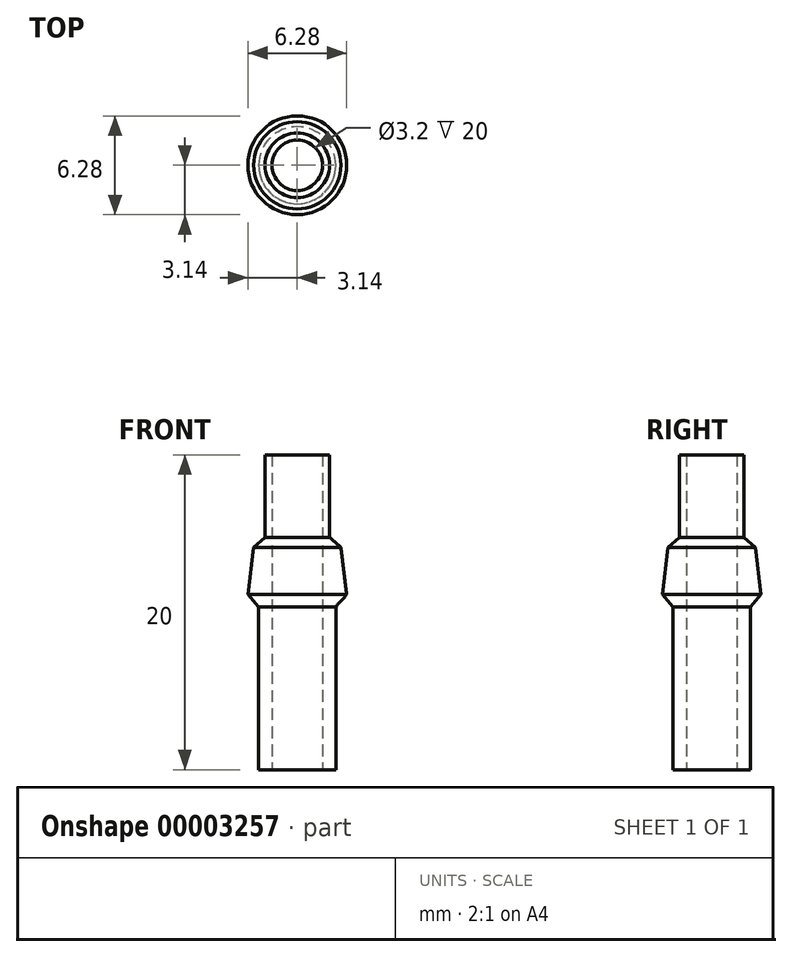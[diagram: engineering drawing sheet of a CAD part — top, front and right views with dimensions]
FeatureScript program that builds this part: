
annotation { "Feature Type Name" : "Feature", "Feature Type Description" : "" }
export const myFeature = defineFeature(function(context is Context, id is Id, definition is map)
    precondition{}
    {
        {
            var Q0;
            Q0=qCreatedBy(makeId("Top.planeOp"),FACE);
            var sketch = newSketch(context, id + "F0", { "sketchPlane" : qUnion([Q0])});
            skCircle(sketch, "E0", {"center": v(0, 0) * mm, "radius": 4.5 * mm});
            skSolve(sketch);
        }
        {
            var Q0;
            Q0=qCreatedBy(makeId("Top.planeOp"),FACE);
            cPlane(context, id + "F1", {"entities" : qUnion([Q0]), "cplaneType" : CPlaneType.OFFSET, "offset" : 20 * mm, "width" : 150 * mm, "height" : 150 * mm});
        }
        {
            var Q0;
            Q0=qCreatedBy(id+"F1.planeOp",FACE);
            var sketch = newSketch(context, id + "F2", { "sketchPlane" : qUnion([Q0])});
            skCircle(sketch, "E1", {"center": v(0, 0) * mm, "radius": 2.05 * mm});
            skSolve(sketch);
        }
        {
            var Q0;
            Q0=makeQuery(id+"F0.imprint","IMPRINT",FACE,{"disambiguationData":[TD([[makeQuery(id+"F0.imprint","IMPRINT",EDGE,{"derivedFrom":sQuery(id+"F0.wireOp",EDGE,"E0")}),1.0]])]});
            var Q1;
            Q1=makeQuery(id+"F2.imprint","IMPRINT",FACE,{"disambiguationData":[TD([[makeQuery(id+"F2.imprint","IMPRINT",EDGE,{"derivedFrom":sQuery(id+"F2.wireOp",EDGE,"E1")}),1.0]])]});
            loft(context, id + "F3", {"sheetProfilesArray" : [{ "sheetProfileEntities" : qUnion([Q0]) }, { "sheetProfileEntities" : qUnion([Q1]) }]});
        }
        {
            var Q0;
            Q0=makeQuery(id+"F3.opLoft","CAP_FACE",FACE,{"disambiguationData":[OSD([makeQuery(id+"F0.imprint","IMPRINT",FACE,{"disambiguationData":[TD([[makeQuery(id+"F0.imprint","IMPRINT",EDGE,{"derivedFrom":sQuery(id+"F0.wireOp",EDGE,"E0")}),1.0]])]})])],"isStart":true});
            var sketch = newSketch(context, id + "F4", { "sketchPlane" : qUnion([Q0])});
            skCircle(sketch, "E2", {"center": v(0, 0) * mm, "radius": 1.6 * mm});
            skSolve(sketch);
        }
        {
            var Q0;
            Q0=makeQuery(id+"F4.imprint","IMPRINT",FACE,{"disambiguationData":[TD([[makeQuery(id+"F4.imprint","IMPRINT",EDGE,{"derivedFrom":sQuery(id+"F4.wireOp",EDGE,"E2")}),1.0]])]});
            extrude(context, id + "F5", {"entities" : qUnion([Q0]), "operationType" : NewBodyOperationType.REMOVE, "oppositeDirection" : true, "depth" : 25 * mm});
        }
        {
            var Q0;
            Q0=makeQuery(id+"F3.opLoft","CAP_FACE",FACE,{"disambiguationData":[OSD([makeQuery(id+"F2.imprint","IMPRINT",FACE,{"disambiguationData":[TD([[makeQuery(id+"F2.imprint","IMPRINT",EDGE,{"derivedFrom":sQuery(id+"F2.wireOp",EDGE,"E1")}),1.0]])]})])],"isStart":true});
            var sketch = newSketch(context, id + "F6", { "sketchPlane" : qUnion([Q0])});
            skCircle(sketch, "E3.0", {"center": v(0, 0) * mm, "radius": 2.05 * mm});
            skCircle(sketch, "E4", {"center": v(0, 0) * mm, "radius": 2.77 * mm});
            skSolve(sketch);
        }
        {
            var Q0;
            Q0=makeQuery(id+"F6.imprint","IMPRINT",FACE,{"disambiguationData":[TD([[makeQuery(id+"F6.imprint","IMPRINT",EDGE,{"derivedFrom":sQuery(id+"F6.wireOp",EDGE,"E3.0")}),-1.0]])]});
            extrude(context, id + "F7", {"entities" : qUnion([Q0]), "operationType" : NewBodyOperationType.REMOVE, "oppositeDirection" : true, "depth" : 5 * mm});
        }
        {
            var Q0;
            Q0=makeQuery(id+"F3.opLoft","CAP_FACE",FACE,{"disambiguationData":[OSD([makeQuery(id+"F0.imprint","IMPRINT",FACE,{"disambiguationData":[TD([[makeQuery(id+"F0.imprint","IMPRINT",EDGE,{"derivedFrom":sQuery(id+"F0.wireOp",EDGE,"E0")}),1.0]])]})])],"isStart":true});
            var sketch = newSketch(context, id + "F8", { "sketchPlane" : qUnion([Q0])});
            skCircle(sketch, "E5", {"center": v(0, 0) * mm, "radius": 2.45 * mm});
            skCircle(sketch, "E6", {"center": v(0, 0) * mm, "radius": 7.1 * mm});
            skSolve(sketch);
        }
        {
            var Q0;
            Q0=makeQuery(id+"F8.imprint","IMPRINT",FACE,{"disambiguationData":[TD([[makeQuery(id+"F8.imprint","IMPRINT",EDGE,{"derivedFrom":sQuery(id+"F8.wireOp",EDGE,"E5")}),-1.0]])]});
            extrude(context, id + "F9", {"entities" : qUnion([Q0]), "operationType" : NewBodyOperationType.REMOVE, "oppositeDirection" : true, "depth" : 10 * mm});
        }
        {
            var Q0;
            {var subQ0=sQuery(id+"F0.wireOp",EDGE,"E0");Q0=makeQuery(id+"F9.boolean.opBoolean","INTERSECT",EDGE,{"derivedFrom":[makeQuery(id+"F3.opLoft","SWEPT_FACE",FACE,{"disambiguationData":[OSD([subQ0,sQuery(id+"F2.wireOp",EDGE,"E1")])]}),makeQuery(id+"F9.opExtrude","CAP_FACE",FACE,{"disambiguationData":[OSD([subQ0,sQuery(id+"F8.wireOp",EDGE,"E5")])],"isStart":false})]});}
            var Q1;
            Q1=makeQuery(id+"F7.boolean.opBoolean","INTERSECT",EDGE,{"derivedFrom":[makeQuery(id+"F3.opLoft","SWEPT_FACE",FACE,{"disambiguationData":[OSD([sQuery(id+"F0.wireOp",EDGE,"E0"),sQuery(id+"F2.wireOp",EDGE,"E1")])]}),makeQuery(id+"F7.opExtrude","CAP_FACE",FACE,{"disambiguationData":[OSD([sQuery(id+"F6.wireOp",EDGE,"E3.0"),sQuery(id+"F6.wireOp",EDGE,"E4")])],"isStart":false})]});
            chamfer(context, id + "F10", {"entities" : qUnion([Q0, Q1]), "width" : 1 * mm, "tangentPropagation" : true});
        }
    });
